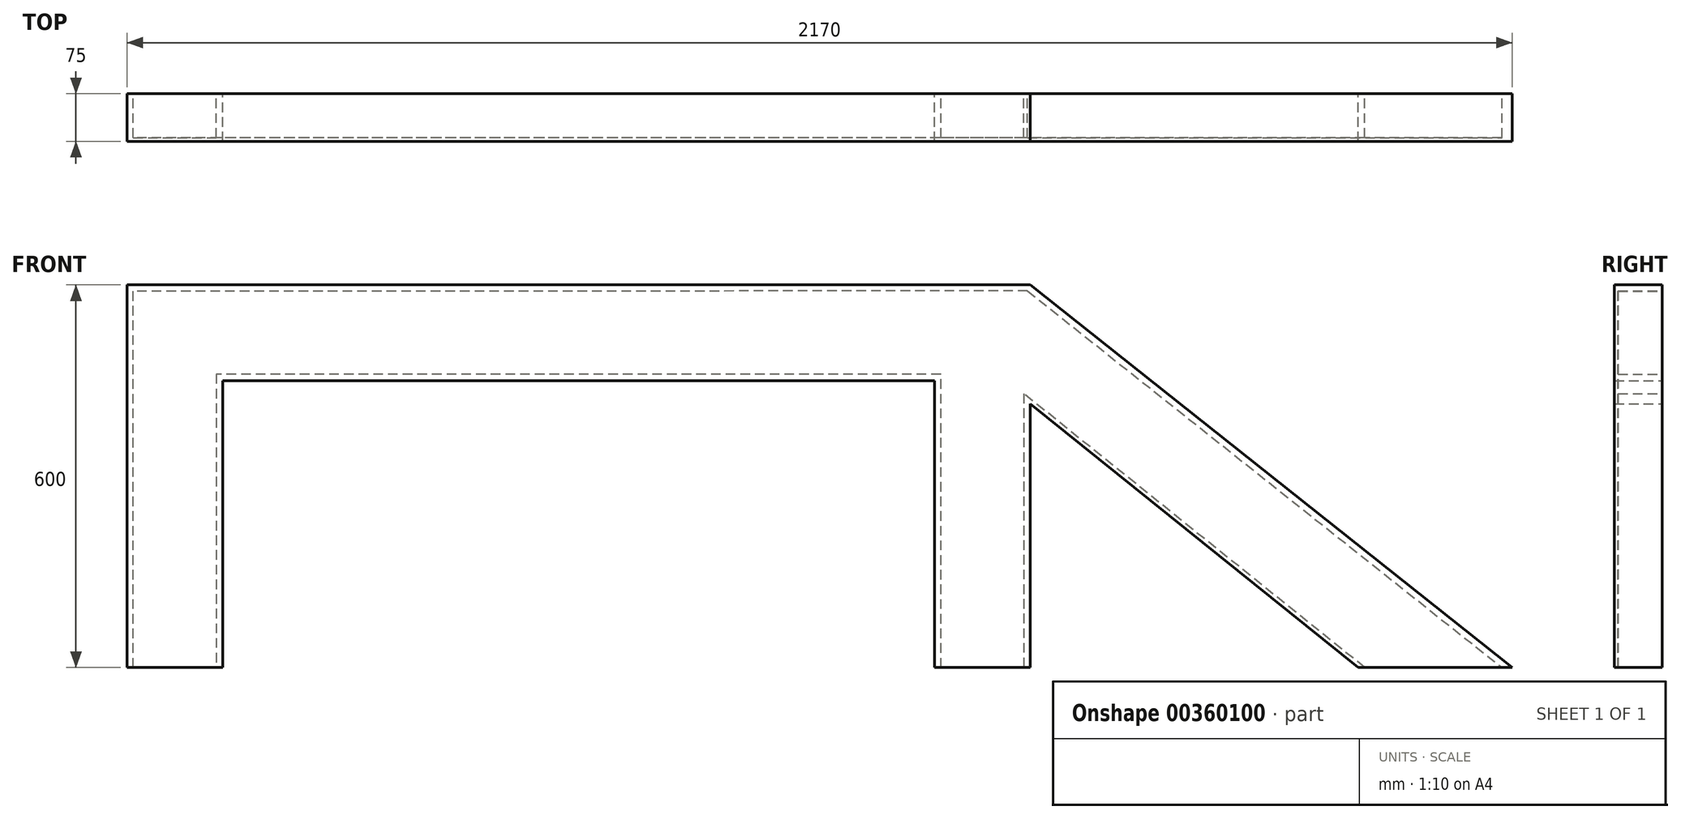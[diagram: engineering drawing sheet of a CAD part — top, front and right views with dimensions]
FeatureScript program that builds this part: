
annotation { "Feature Type Name" : "Feature", "Feature Type Description" : "" }
export const myFeature = defineFeature(function(context is Context, id is Id, definition is map)
    precondition{}
    {
        {
            var Q0;
            Q0=qCreatedBy(makeId("Front.planeOp"),FACE);
            var sketch = newSketch(context, id + "F0", { "sketchPlane" : qUnion([Q0])});
            skLineSegment(sketch, "E0", {"start": v(0, 0) * mm, "end": v(0, 600) * mm});
            skLineSegment(sketch, "E1", {"start": v(0, 600) * mm, "end": v(1415, 600) * mm});
            skLineSegment(sketch, "E2", {"start": v(2170, 0) * mm, "end": v(1415, 600) * mm});
            skLineSegment(sketch, "E3", {"start": v(0, 0) * mm, "end": v(150, 0) * mm});
            skLineSegment(sketch, "E4", {"start": v(1415, 0) * mm, "end": v(1265, 0) * mm});
            skLineSegment(sketch, "E5", {"start": v(1265, 0) * mm, "end": v(1265, 450) * mm});
            skLineSegment(sketch, "E6", {"start": v(150, 0) * mm, "end": v(150, 450) * mm});
            skLineSegment(sketch, "E7", {"start": v(150, 450) * mm, "end": v(1265, 450) * mm});
            skLineSegment(sketch, "E8", {"start": v(1415, 413.25) * mm, "end": v(1415, 0) * mm});
            skLineSegment(sketch, "E9", {"start": v(2170, 0) * mm, "end": v(1928.9, 0) * mm});
            skLineSegment(sketch, "E10", {"start": v(1928.9, 0) * mm, "end": v(1415, 413.25) * mm});
            skSolve(sketch);
        }
        {
            var Q0;
            Q0=qSketchRegion(id+"F0",true);
            extrude(context, id + "F1", {"entities" : qUnion([Q0]), "depth" : 75 * mm});
        }
        {
            var Q0;
            Q0=makeQuery(id+"F1.opExtrude","CAP_FACE",FACE,{"disambiguationData":[OSD([sQuery(id+"F0.wireOp",EDGE,"E0"),sQuery(id+"F0.wireOp",EDGE,"E1"),sQuery(id+"F0.wireOp",EDGE,"E2"),sQuery(id+"F0.wireOp",EDGE,"E3"),sQuery(id+"F0.wireOp",EDGE,"E4"),sQuery(id+"F0.wireOp",EDGE,"E5"),sQuery(id+"F0.wireOp",EDGE,"E6"),sQuery(id+"F0.wireOp",EDGE,"E7"),sQuery(id+"F0.wireOp",EDGE,"E8"),sQuery(id+"F0.wireOp",EDGE,"E9"),sQuery(id+"F0.wireOp",EDGE,"E10")])],"isStart":true});
            var sketch = newSketch(context, id + "F2", { "sketchPlane" : qUnion([Q0])});
            skLineSegment(sketch, "E11", {"start": v(-1275, 0) * mm, "end": v(-1275, 460) * mm});
            skLineSegment(sketch, "E12", {"start": v(-1275, 460) * mm, "end": v(-140, 460) * mm});
            skLineSegment(sketch, "E13", {"start": v(-140, 460) * mm, "end": v(-140, 0) * mm});
            skLineSegment(sketch, "E14", {"start": v(-10, 0) * mm, "end": v(-10, 590) * mm});
            skLineSegment(sketch, "E15", {"start": v(-1411.51, 590) * mm, "end": v(-1410.82, 590.52) * mm});
            skLineSegment(sketch, "E16", {"start": v(-1410.82, 590.52) * mm, "end": v(-2153.82, 0) * mm});
            skLineSegment(sketch, "E17", {"start": v(-1410.82, 590.52) * mm, "end": v(-10, 590) * mm});
            skLineSegment(sketch, "E18", {"start": v(-1938.9, 0) * mm, "end": v(-1405, 429.33) * mm});
            skLineSegment(sketch, "E19", {"start": v(-1405, 429.33) * mm, "end": v(-1405, 0) * mm});
            skLineSegment(sketch, "E20", {"start": v(-2153.82, 0) * mm, "end": v(-1938.9, 0) * mm});
            skLineSegment(sketch, "E21", {"start": v(-1405, 0) * mm, "end": v(-1275, 0) * mm});
            skLineSegment(sketch, "E22", {"start": v(-140, 0) * mm, "end": v(-10, 0) * mm});
            skSolve(sketch);
        }
        {
            var Q0;
            Q0 = qSketchRegion(id + "F2", true);
            extrude(context, id + "F3", {"entities" : qUnion([Q0]), "operationType" : NewBodyOperationType.REMOVE, "oppositeDirection" : true, "depth" : 69 * mm});
        }
    });
